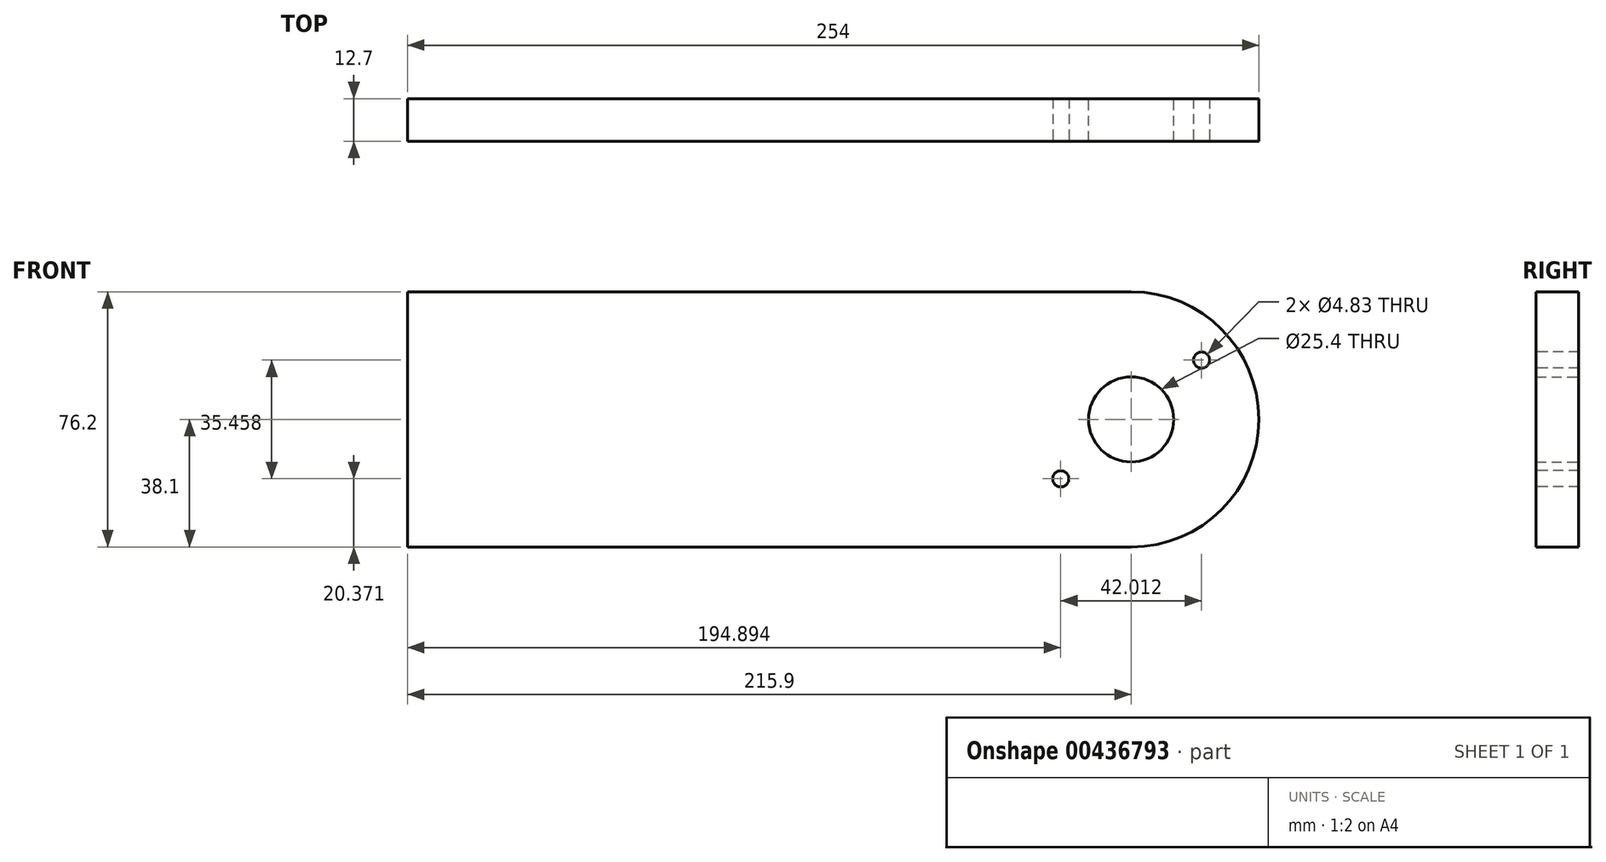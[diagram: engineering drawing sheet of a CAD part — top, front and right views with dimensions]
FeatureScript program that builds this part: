
annotation { "Feature Type Name" : "Feature", "Feature Type Description" : "" }
export const myFeature = defineFeature(function(context is Context, id is Id, definition is map)
    precondition{}
    {
        {
            var Q0;
            Q0=qCreatedBy(makeId("Front.planeOp"),FACE);
            var sketch = newSketch(context, id + "F0", { "sketchPlane" : qUnion([Q0])});
            skLineSegment(sketch, "E0.bottom", {"start": v(0, 0) * mm, "end": v(215.9, 0) * mm});
            skLineSegment(sketch, "E0.top", {"start": v(0, 76.2) * mm, "end": v(215.9, 76.2) * mm});
            skLineSegment(sketch, "E0.left", {"start": v(0, 0) * mm, "end": v(0, 76.2) * mm});
            skLineSegment(sketch, "E0.right", {"start": v(254, 38.1) * mm, "end": v(254, 38.1) * mm});
            skLineSegment(sketch, "E1", {"start": v(0, 38.1) * mm, "end": v(215.9, 38.1) * mm});
            skPoint(sketch, "E1.endSnap0", {"position": v(254, 38.1) * mm});
            skCircle(sketch, "E2", {"center": v(215.9, 38.1) * mm, "radius": 12.7 * mm});
            skPoint(sketch, "E3.visualSharp", {"position": v(254, 76.2) * mm});
            skArc(sketch, "E3.filletArc", {"start": v(254, 38.1) * mm, "mid": v(242.84, 65.04) * mm, "end": v(215.9, 76.2) * mm});
            skPoint(sketch, "E4.visualSharp", {"position": v(254, 0) * mm});
            skArc(sketch, "E4.filletArc", {"start": v(215.9, 0) * mm, "mid": v(242.84, 11.16) * mm, "end": v(254, 38.1) * mm});
            skSolve(sketch);
        }
        {
            var Q0;
            {var subQ3=sQuery(id+"F0.wireOp",EDGE,"E0.bottom");Q0=makeQuery(id+"F0.imprint","IMPRINT",FACE,{"disambiguationData":[TD([[makeQuery(id+"F0.imprint","IMPRINT",EDGE,{"derivedFrom":subQ3}),1.0]])]});}
            extrude(context, id + "F1", {"entities" : qUnion([Q0]), "depth" : 12.7 * mm});
        }
        {
            var Q0;
            Q0=makeQuery(id+"F1.opExtrude","CAP_FACE",FACE,{"disambiguationData":[OSD([sQuery(id+"F0.wireOp",EDGE,"E0.bottom"),sQuery(id+"F0.wireOp",EDGE,"E0.top"),sQuery(id+"F0.wireOp",EDGE,"E0.left"),sQuery(id+"F0.wireOp",EDGE,"E2"),sQuery(id+"F0.wireOp",EDGE,"E3.filletArc"),sQuery(id+"F0.wireOp",EDGE,"E4.filletArc")])],"isStart":false});
            var sketch = newSketch(context, id + "F2", { "sketchPlane" : qUnion([Q0])});
            skLineSegment(sketch, "E5", {"start": v(215.9, 38.1) * mm, "end": v(194.9, 38.1) * mm});
            skLineSegment(sketch, "E6", {"start": v(194.9, 38.1) * mm, "end": v(194.9, 55.83) * mm});
            skLineSegment(sketch, "E7", {"start": v(194.9, 55.83) * mm, "end": v(236.9, 55.83) * mm});
            skLineSegment(sketch, "E8", {"start": v(236.9, 55.83) * mm, "end": v(236.9, 20.37) * mm});
            skLineSegment(sketch, "E9", {"start": v(236.9, 20.37) * mm, "end": v(194.9, 20.37) * mm});
            skLineSegment(sketch, "E10", {"start": v(194.9, 20.37) * mm, "end": v(194.9, 38.1) * mm});
            skCircle(sketch, "E11", {"center": v(236.9, 55.83) * mm, "radius": 2.41 * mm});
            skCircle(sketch, "E12", {"center": v(194.9, 20.37) * mm, "radius": 2.41 * mm});
            skSolve(sketch);
        }
        {
            var Q0;
            {var subQ0=sQuery(id+"F2.wireOp",EDGE,"E10");var subQ1=sQuery(id+"F2.wireOp",EDGE,"E9");var subQ2=makeQuery(id+"F2.imprint","INTERSECT",VERTEX,{"derivedFrom":[subQ1,subQ0]});Q0=makeQuery(id+"F2.imprint","IMPRINT",FACE,{"disambiguationData":[TD([[makeQuery(id+"F2.imprint","IMPRINT",EDGE,{"disambiguationData":[TD([[subQ2,1.0]])],"derivedFrom":subQ1}),1.0]])]});}
            var Q1;
            {var subQ0=sQuery(id+"F2.wireOp",EDGE,"E10");var subQ1=sQuery(id+"F2.wireOp",EDGE,"E9");var subQ2=makeQuery(id+"F2.imprint","INTERSECT",VERTEX,{"derivedFrom":[subQ1,subQ0]});Q1=makeQuery(id+"F2.imprint","IMPRINT",FACE,{"disambiguationData":[TD([[makeQuery(id+"F2.imprint","IMPRINT",EDGE,{"disambiguationData":[TD([[subQ2,1.0]])],"derivedFrom":subQ1}),-1.0]])]});}
            var Q2;
            {var subQ0=sQuery(id+"F2.wireOp",EDGE,"E8");var subQ1=sQuery(id+"F2.wireOp",EDGE,"E7");var subQ2=makeQuery(id+"F2.imprint","INTERSECT",VERTEX,{"derivedFrom":[subQ1,subQ0]});Q2=makeQuery(id+"F2.imprint","IMPRINT",FACE,{"disambiguationData":[TD([[makeQuery(id+"F2.imprint","IMPRINT",EDGE,{"disambiguationData":[TD([[subQ2,1.0]])],"derivedFrom":subQ1}),-1.0]])]});}
            var Q3;
            {var subQ0=sQuery(id+"F2.wireOp",EDGE,"E8");var subQ1=sQuery(id+"F2.wireOp",EDGE,"E7");var subQ2=makeQuery(id+"F2.imprint","INTERSECT",VERTEX,{"derivedFrom":[subQ1,subQ0]});Q3=makeQuery(id+"F2.imprint","IMPRINT",FACE,{"disambiguationData":[TD([[makeQuery(id+"F2.imprint","IMPRINT",EDGE,{"disambiguationData":[TD([[subQ2,1.0]])],"derivedFrom":subQ1}),1.0]])]});}
            extrude(context, id + "F3", {"entities" : qUnion([Q0, Q1, Q2, Q3]), "operationType" : NewBodyOperationType.REMOVE, "oppositeDirection" : true, "depth" : 25.4 * mm});
        }
    });
